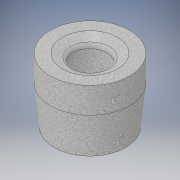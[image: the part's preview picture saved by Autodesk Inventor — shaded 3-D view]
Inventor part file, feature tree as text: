
AUTODESK INVENTOR PART (.ipt)
format: ipt  version: 2017 SP1 (Build 210196100, 196)  size: 174,080 bytes
history: native  units: in
note: dims shown in document units (in); Inventor stores cm internally (conversion verified against a paired STEP export)
features: revolve x1, sketch x1
ambient origin geometry x8: Origin, YZ Plane, XZ Plane, XY Plane, X Axis, Y Axis, Z Axis, Center Point
bodies: Solid1 (feature_tree)
feature tree (2):
  revolve  "Revolution1"  [1 undecoded]
  sketch  "Sketch1"  dims[d0=0.5in d1=1.13in d3=15.0deg d4=0.25in d9=1.5in d11=0.5in d13=3.75in d14=0.25in d15=1.0in d16=0.25in d17=0.5in d18=0.234in d19=0.234in d20=0.5in d22=4.25in d23=2.5in d25=1.0in d26=0.25in d27=5.25in d28=0.125in d29=4.0in d30=0.25in d31=0.1718in d32=1.75in d33=0.125in d34=0.801in d35=0.375in d37=90.0deg]
note: 1 required parameter value undecoded (feature->parameter linkage not recoverable at this tier; creation-order binding heuristic only, values carry confidence <= 0.55)
